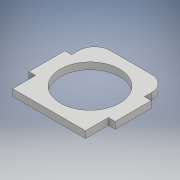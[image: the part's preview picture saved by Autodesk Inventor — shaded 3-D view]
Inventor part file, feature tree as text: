
AUTODESK INVENTOR PART (.ipt)
format: ipt  version: 2018 (Build 220112000, 112)  size: 118,272 bytes
history: native  units: mm
features: other x1, extrude x1, sketch x1
ambient origin geometry x8: Origin, YZ Plane, XZ Plane, XY Plane, X Axis, Y Axis, Z Axis, Center Point
bodies: Body1 (feature_tree)
feature tree (3):
  other  "Sólido1"
  extrude  "Extrusión1"  Depth=3.0mm TaperAngle=0.0deg
  sketch  "Boceto1"  dims[d12=7.0mm d13=3.0mm d14=0.0mm d15=32.35mm d16=29.35mm d17=8.0mm d18=10.175mm]
